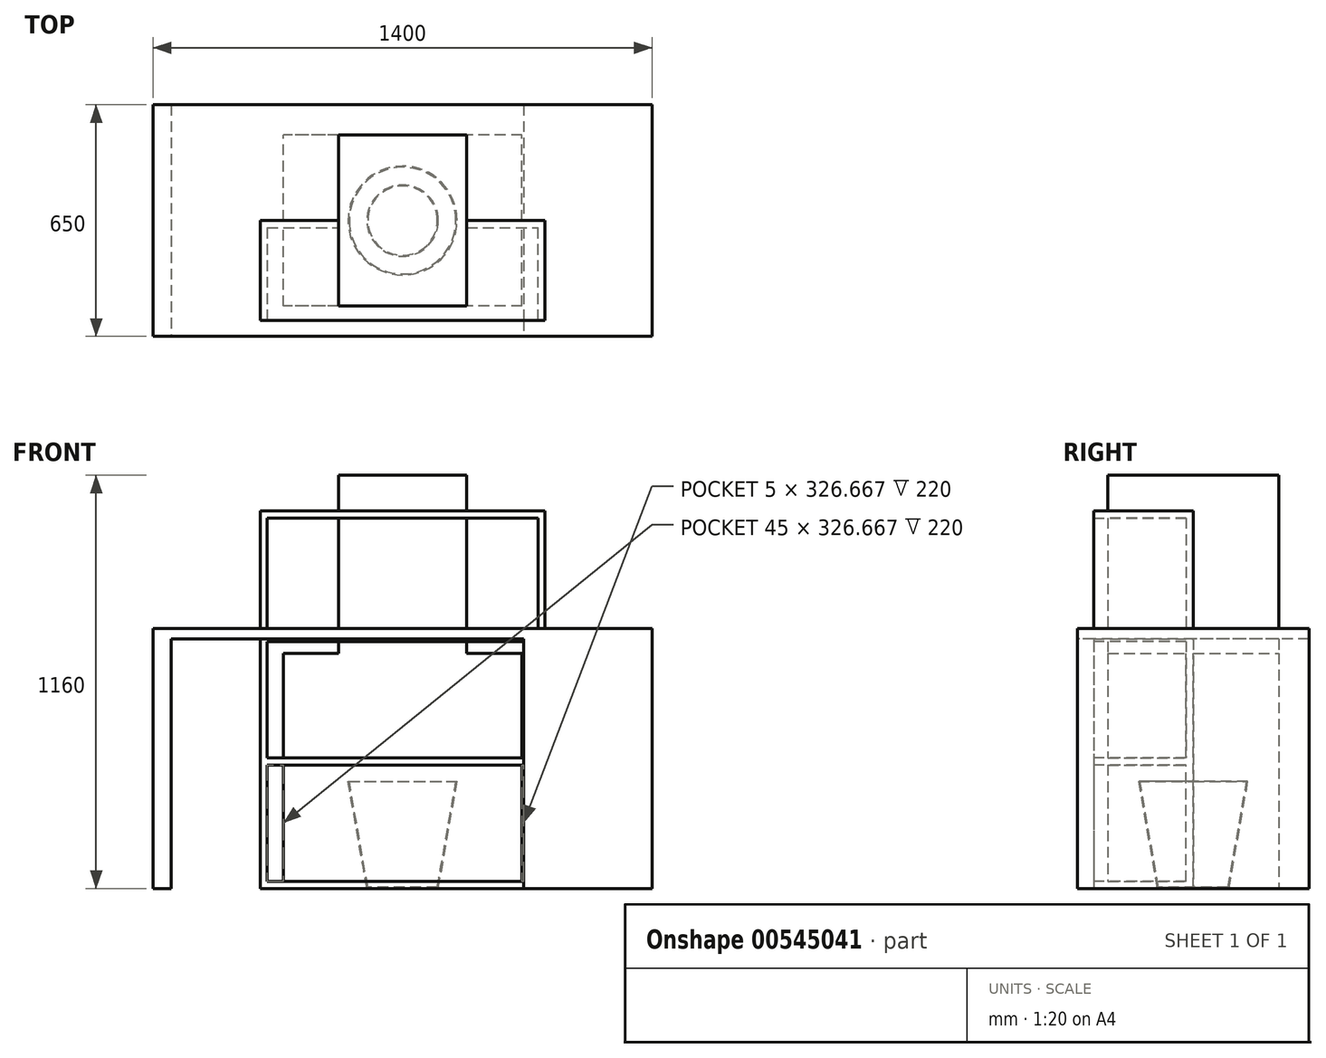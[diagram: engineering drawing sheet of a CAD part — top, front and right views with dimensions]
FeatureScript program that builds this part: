
annotation { "Feature Type Name" : "Feature", "Feature Type Description" : "" }
export const myFeature = defineFeature(function(context is Context, id is Id, definition is map)
    precondition{}
    {
        {
            var Q0;
            Q0=qCreatedBy(makeId("Top.planeOp"),FACE);
            var sketch = newSketch(context, id + "F0", { "sketchPlane" : qUnion([Q0])});
            skLineSegment(sketch, "E0.bottom", {"start": v(335, -240) * mm, "end": v(-335, -240) * mm});
            skLineSegment(sketch, "E0.top", {"start": v(335, 240) * mm, "end": v(-335, 240) * mm});
            skLineSegment(sketch, "E0.left", {"start": v(335, -240) * mm, "end": v(335, 240) * mm});
            skLineSegment(sketch, "E0.right", {"start": v(-335, -240) * mm, "end": v(-335, 240) * mm});
            skPoint(sketch, "E0.middle", {"position": v(0, 0) * mm});
            skSolve(sketch);
        }
        {
            var Q0;
            Q0 = qSketchRegion(id + "F0", true);
            var Q1;
            Q1=makeQuery(id+"F0.imprint","IMPRINT",FACE,{"disambiguationData":[TD([[makeQuery(id+"F0.imprint","IMPRINT",EDGE,{"derivedFrom":sQuery(id+"F0.wireOp",EDGE,"E0.bottom")}),-1.0]])]});
            extrude(context, id + "F1", {"entities" : qUnion([Q0, Q1]), "depth" : 660 * mm, "offsetDistance" : 25 * mm});
        }
        {
            var Q0;
            Q0=qCreatedBy(makeId("Top.planeOp"),FACE);
            var sketch = newSketch(context, id + "F2", { "sketchPlane" : qUnion([Q0])});
            skLineSegment(sketch, "E1.bottom", {"start": v(-180, 240) * mm, "end": v(180, 240) * mm});
            skLineSegment(sketch, "E1.top", {"start": v(-180, -240) * mm, "end": v(180, -240) * mm});
            skLineSegment(sketch, "E1.left", {"start": v(-180, 240) * mm, "end": v(-180, -240) * mm});
            skLineSegment(sketch, "E1.right", {"start": v(180, 240) * mm, "end": v(180, -240) * mm});
            skPoint(sketch, "E1.middle", {"position": v(0, 0) * mm});
            skSolve(sketch);
        }
        {
            var Q0;
            Q0 = qSketchRegion(id + "F2", true);
            extrude(context, id + "F3", {"entities" : qUnion([Q0]), "depth" : 1160 * mm, "offsetDistance" : 25 * mm});
        }
        {
            var Q0;
            Q0=qCreatedBy(makeId("Top.planeOp"),FACE);
            var sketch = newSketch(context, id + "F4", { "sketchPlane" : qUnion([Q0])});
            skLineSegment(sketch, "E2.bottom", {"start": v(-700, 325) * mm, "end": v(700, 325) * mm, "construction": true});
            skLineSegment(sketch, "E2.top", {"start": v(-700, -325) * mm, "end": v(700, -325) * mm, "construction": true});
            skLineSegment(sketch, "E2.left", {"start": v(-700, 325) * mm, "end": v(-700, -325) * mm, "construction": true});
            skLineSegment(sketch, "E2.right", {"start": v(700, 325) * mm, "end": v(700, -325) * mm, "construction": true});
            skPoint(sketch, "E2.middle", {"position": v(0, 0) * mm});
            skLineSegment(sketch, "E3.bottom", {"start": v(700, 325) * mm, "end": v(340, 325) * mm});
            skLineSegment(sketch, "E3.top", {"start": v(700, -325) * mm, "end": v(340, -325) * mm});
            skLineSegment(sketch, "E3.left", {"start": v(700, 325) * mm, "end": v(700, -325) * mm});
            skLineSegment(sketch, "E3.right", {"start": v(340, 325) * mm, "end": v(340, -325) * mm});
            skLineSegment(sketch, "E4.bottom", {"start": v(-700, 325) * mm, "end": v(-650, 325) * mm});
            skLineSegment(sketch, "E4.top", {"start": v(-700, -325) * mm, "end": v(-650, -325) * mm});
            skLineSegment(sketch, "E4.left", {"start": v(-700, 325) * mm, "end": v(-700, -325) * mm});
            skLineSegment(sketch, "E4.right", {"start": v(-650, 325) * mm, "end": v(-650, -325) * mm});
            skSolve(sketch);
        }
        {
            var Q0;
            Q0=makeQuery(id+"F4.imprint","IMPRINT",FACE,{"disambiguationData":[TD([[makeQuery(id+"F4.imprint","IMPRINT",EDGE,{"derivedFrom":sQuery(id+"F4.wireOp",EDGE,"E3.bottom")}),1.0]])]});
            var Q1;
            Q1=makeQuery(id+"F4.imprint","IMPRINT",FACE,{"disambiguationData":[TD([[makeQuery(id+"F4.imprint","IMPRINT",EDGE,{"derivedFrom":sQuery(id+"F4.wireOp",EDGE,"E4.bottom")}),-1.0]])]});
            extrude(context, id + "F5", {"entities" : qUnion([Q0, Q1]), "depth" : 700 * mm, "offsetDistance" : 25 * mm});
        }
        {
            var Q0;
            Q0=makeQuery(id+"F5.opExtrude","CAP_FACE",FACE,{"disambiguationData":[OSD([sQuery(id+"F4.wireOp",EDGE,"E3.bottom"),sQuery(id+"F4.wireOp",EDGE,"E3.top"),sQuery(id+"F4.wireOp",EDGE,"E3.left"),sQuery(id+"F4.wireOp",EDGE,"E3.right")])],"isStart":false});
            var sketch = newSketch(context, id + "F6", { "sketchPlane" : qUnion([Q0])});
            skLineSegment(sketch, "E5.bottom", {"start": v(700, 325) * mm, "end": v(-700, 325) * mm});
            skLineSegment(sketch, "E5.top", {"start": v(700, -325) * mm, "end": v(-700, -325) * mm});
            skLineSegment(sketch, "E5.left", {"start": v(700, 325) * mm, "end": v(700, -325) * mm});
            skLineSegment(sketch, "E5.right", {"start": v(-700, 325) * mm, "end": v(-700, -325) * mm});
            skSolve(sketch);
        }
        {
            var Q0;
            {var subQ2=sQuery(id+"F6.wireOp",EDGE,"E5.right");Q0=makeQuery(id+"F6.imprint","IMPRINT",FACE,{"disambiguationData":[TD([[makeQuery(id+"F6.imprint","IMPRINT",EDGE,{"derivedFrom":subQ2}),1.0]])]});}
            var Q1;
            {var subQ0=sQuery(id+"F6.wireOp",EDGE,"E5.left");Q1=makeQuery(id+"F6.imprint","IMPRINT",FACE,{"disambiguationData":[TD([[makeQuery(id+"F6.imprint","IMPRINT",EDGE,{"derivedFrom":subQ0}),-1.0]])]});}
            extrude(context, id + "F7", {"entities" : qUnion([Q0, Q1]), "operationType" : NewBodyOperationType.ADD, "depth" : 30 * mm, "offsetDistance" : 25 * mm});
        }
        {
            var Q0;
            Q0=qCreatedBy(makeId("Front.planeOp"),FACE);
            var sketch = newSketch(context, id + "F8", { "sketchPlane" : qUnion([Q0])});
            skLineSegment(sketch, "E6.bottom", {"start": v(-400, 1060) * mm, "end": v(400, 1060) * mm});
            skLineSegment(sketch, "E6.top", {"start": v(-400, 0) * mm, "end": v(400, 0) * mm});
            skLineSegment(sketch, "E6.left", {"start": v(-400, 1060) * mm, "end": v(-400, 0) * mm});
            skLineSegment(sketch, "E6.right", {"start": v(400, 1060) * mm, "end": v(400, 0) * mm});
            skLineSegment(sketch, "E7", {"start": v(-380, 1040) * mm, "end": v(380, 1040) * mm});
            skLineSegment(sketch, "E8", {"start": v(380, 1040) * mm, "end": v(380, 713.33) * mm});
            skLineSegment(sketch, "E9", {"start": v(380, 713.33) * mm, "end": v(-380, 713.33) * mm});
            skLineSegment(sketch, "E10", {"start": v(-380, 713.33) * mm, "end": v(-380, 1040) * mm});
            skLineSegment(sketch, "E11.bottom", {"start": v(-380, 693.33) * mm, "end": v(380, 693.33) * mm});
            skLineSegment(sketch, "E11.top", {"start": v(-380, 366.67) * mm, "end": v(380, 366.67) * mm});
            skLineSegment(sketch, "E11.left", {"start": v(-380, 693.33) * mm, "end": v(-380, 366.67) * mm});
            skLineSegment(sketch, "E11.right", {"start": v(380, 693.33) * mm, "end": v(380, 366.67) * mm});
            skLineSegment(sketch, "E12.bottom", {"start": v(-380, 346.67) * mm, "end": v(380, 346.67) * mm});
            skLineSegment(sketch, "E12.top", {"start": v(-380, 20) * mm, "end": v(380, 20) * mm});
            skLineSegment(sketch, "E12.left", {"start": v(-380, 346.67) * mm, "end": v(-380, 20) * mm});
            skLineSegment(sketch, "E12.right", {"start": v(380, 346.67) * mm, "end": v(380, 20) * mm});
            skSolve(sketch);
        }
        {
            var Q0;
            Q0=makeQuery(id+"F8.imprint","IMPRINT",FACE,{"disambiguationData":[TD([[makeQuery(id+"F8.imprint","IMPRINT",EDGE,{"derivedFrom":sQuery(id+"F8.wireOp",EDGE,"E6.bottom")}),-1.0]])]});
            extrude(context, id + "F9", {"entities" : qUnion([Q0]), "depth" : 280 * mm, "offsetDistance" : 25 * mm});
        }
        {
            var Q0;
            Q0=makeQuery(id+"F8.imprint","IMPRINT",FACE,{"disambiguationData":[TD([[makeQuery(id+"F8.imprint","IMPRINT",EDGE,{"derivedFrom":sQuery(id+"F8.wireOp",EDGE,"E6.bottom")}),-1.0]])]});
            var Q1;
            Q1=makeQuery(id+"F8.imprint","IMPRINT",FACE,{"disambiguationData":[TD([[makeQuery(id+"F8.imprint","IMPRINT",EDGE,{"derivedFrom":sQuery(id+"F8.wireOp",EDGE,"E7")}),-1.0]])]});
            var Q2;
            Q2=makeQuery(id+"F8.imprint","IMPRINT",FACE,{"disambiguationData":[TD([[makeQuery(id+"F8.imprint","IMPRINT",EDGE,{"derivedFrom":sQuery(id+"F8.wireOp",EDGE,"E11.bottom")}),-1.0]])]});
            var Q3;
            Q3=makeQuery(id+"F8.imprint","IMPRINT",FACE,{"disambiguationData":[TD([[makeQuery(id+"F8.imprint","IMPRINT",EDGE,{"derivedFrom":sQuery(id+"F8.wireOp",EDGE,"E12.bottom")}),-1.0]])]});
            extrude(context, id + "F10", {"entities" : qUnion([Q0, Q1, Q2, Q3]), "operationType" : NewBodyOperationType.ADD, "depth" : 20 * mm, "offsetDistance" : 25 * mm});
        }
        {
            var Q0;
            Q0=qCreatedBy(makeId("Front.planeOp"),FACE);
            var sketch = newSketch(context, id + "F11", { "sketchPlane" : qUnion([Q0])});
            skLineSegment(sketch, "E13", {"start": v(0, 0) * mm, "end": v(0, 391.65) * mm, "construction": true});
            skLineSegment(sketch, "E14", {"start": v(0, 300) * mm, "end": v(-152.9, 300) * mm});
            skLineSegment(sketch, "E15", {"start": v(-152.9, 300) * mm, "end": v(-100, 0) * mm});
            skLineSegment(sketch, "E16", {"start": v(-100, 0) * mm, "end": v(0, 0) * mm});
            skLineSegment(sketch, "E17", {"start": v(0, 300) * mm, "end": v(0, 0) * mm});
            skSolve(sketch);
        }
        {
            var Q0;
            Q0 = qSketchRegion(id + "F11", true);
            var Q1;
            Q1=sQuery(id+"F11.wireOp",EDGE,"E13");
            revolve(context, id + "F12", {"surfaceOperationType" : NewSurfaceOperationType.NEW, "entities" : qUnion([Q0]), "axis" : qUnion([Q1]), "revolveType" : RevolveType.FULL});
        }
        {
            var Q0;
            Q0=makeQuery(id+"F12.opRevolve","SWEPT_FACE",FACE,{"disambiguationData":[OSD([sQuery(id+"F11.wireOp",EDGE,"E14")])]});
            shell(context, id + "F13", {"entities" : qUnion([Q0]), "thickness" : 3 * mm});
        }
    });
